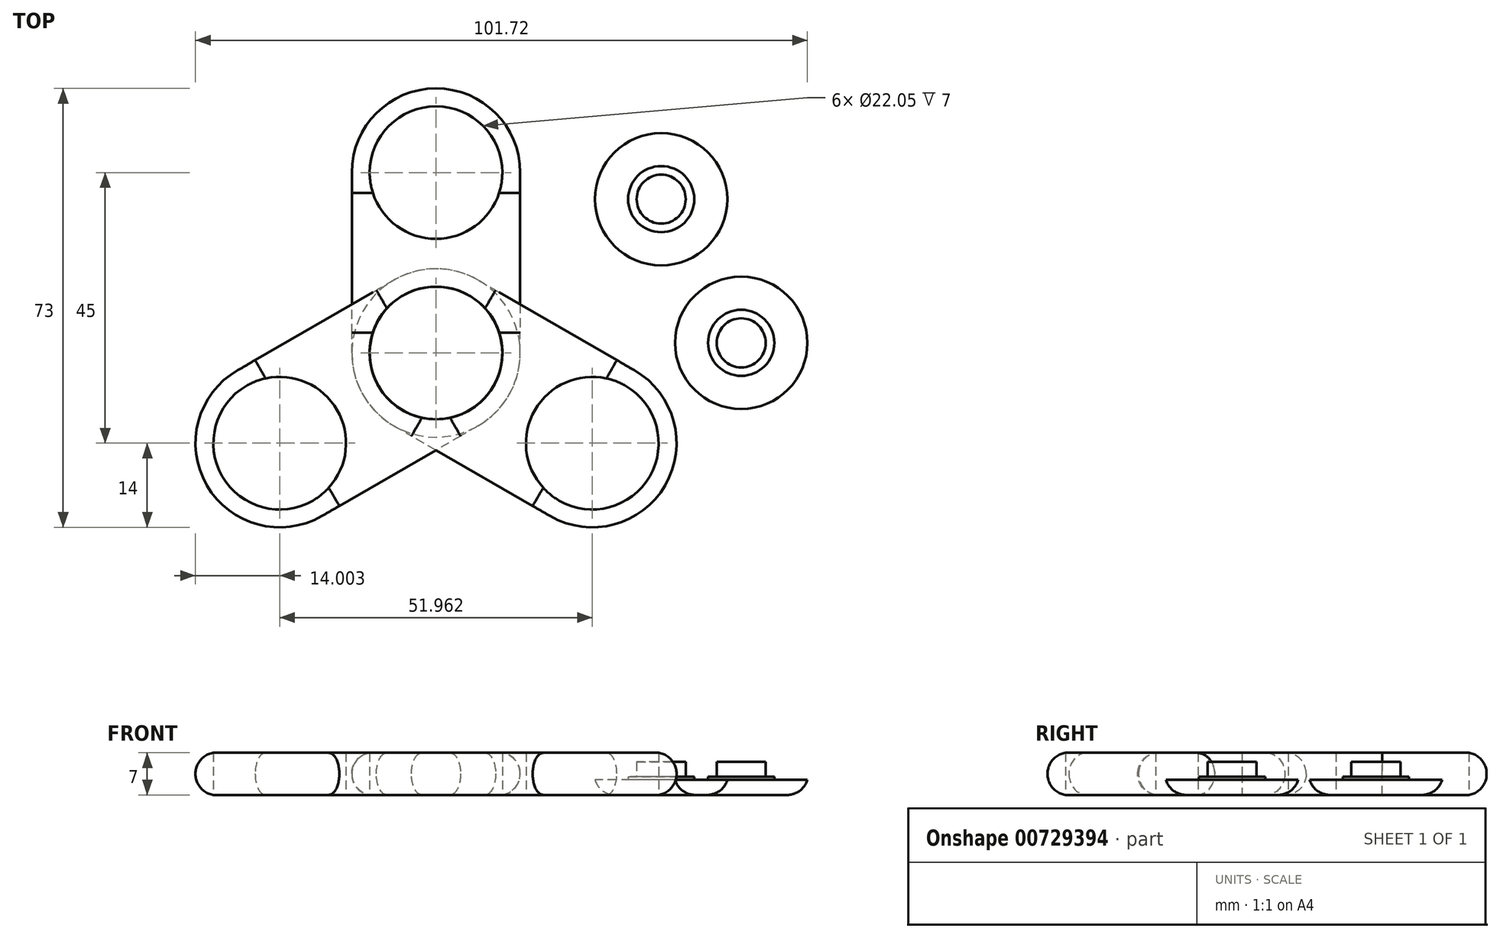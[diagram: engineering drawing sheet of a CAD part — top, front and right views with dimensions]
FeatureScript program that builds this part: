
annotation { "Feature Type Name" : "Feature", "Feature Type Description" : "" }
export const myFeature = defineFeature(function(context is Context, id is Id, definition is map)
    precondition{}
    {
        {
            var Q0;
            Q0=qCreatedBy(makeId("Top.planeOp"),FACE);
            var sketch = newSketch(context, id + "F0", { "sketchPlane" : qUnion([Q0])});
            skLineSegment(sketch, "E0.bottom", {"start": v(-13.49, 0) * mm, "end": v(14.51, 0) * mm});
            skLineSegment(sketch, "E0.top", {"start": v(-13.49, 30) * mm, "end": v(14.51, 30) * mm});
            skLineSegment(sketch, "E0.left", {"start": v(-13.49, 0) * mm, "end": v(-13.49, 30) * mm});
            skLineSegment(sketch, "E0.right", {"start": v(14.51, 0) * mm, "end": v(14.51, 30) * mm});
            skCircle(sketch, "E1", {"center": v(0.51, 30) * mm, "radius": 14 * mm});
            skCircle(sketch, "E2", {"center": v(0.51, 30) * mm, "radius": 11.03 * mm});
            skCircle(sketch, "E3", {"center": v(0.51, 0) * mm, "radius": 14 * mm});
            skCircle(sketch, "E4", {"center": v(0.51, 0) * mm, "radius": 11.03 * mm});
            skSolve(sketch);
        }
        {
            var Q0;
            {var subQ1=sQuery(id+"F0.wireOp",EDGE,"E0.top");var subQ3=sQuery(id+"F0.wireOp",EDGE,"E2");var subQ4=makeQuery(id+"F0.imprint","INTERSECT",VERTEX,{"disambiguationData":[OD(0.0)],"derivedFrom":[subQ1,subQ3]});Q0=makeQuery(id+"F0.imprint","IMPRINT",FACE,{"disambiguationData":[TD([[makeQuery(id+"F0.imprint","IMPRINT",EDGE,{"disambiguationData":[TD([[subQ4,-1.0]])],"derivedFrom":subQ3}),-1.0]])]});}
            var Q1;
            {var subQ1=sQuery(id+"F0.wireOp",EDGE,"E0.top");var subQ3=sQuery(id+"F0.wireOp",EDGE,"E2");var subQ4=makeQuery(id+"F0.imprint","INTERSECT",VERTEX,{"disambiguationData":[OD(0.0)],"derivedFrom":[subQ1,subQ3]});Q1=makeQuery(id+"F0.imprint","IMPRINT",FACE,{"disambiguationData":[TD([[makeQuery(id+"F0.imprint","IMPRINT",EDGE,{"disambiguationData":[TD([[subQ4,1.0]])],"derivedFrom":subQ3}),-1.0]])]});}
            var Q2;
            {var subQ0=sQuery(id+"F0.wireOp",EDGE,"E0.left");Q2=makeQuery(id+"F0.imprint","IMPRINT",FACE,{"disambiguationData":[TD([[makeQuery(id+"F0.imprint","IMPRINT",EDGE,{"derivedFrom":subQ0}),-1.0]])]});}
            var Q3;
            {var subQ1=sQuery(id+"F0.wireOp",EDGE,"E0.bottom");var subQ3=sQuery(id+"F0.wireOp",EDGE,"E4");var subQ4=makeQuery(id+"F0.imprint","INTERSECT",VERTEX,{"disambiguationData":[OD(0.0)],"derivedFrom":[subQ1,subQ3]});Q3=makeQuery(id+"F0.imprint","IMPRINT",FACE,{"disambiguationData":[TD([[makeQuery(id+"F0.imprint","IMPRINT",EDGE,{"disambiguationData":[TD([[subQ4,1.0]])],"derivedFrom":subQ3}),-1.0]])]});}
            var Q4;
            {var subQ1=sQuery(id+"F0.wireOp",EDGE,"E0.bottom");var subQ3=sQuery(id+"F0.wireOp",EDGE,"E4");var subQ4=makeQuery(id+"F0.imprint","INTERSECT",VERTEX,{"disambiguationData":[OD(0.0)],"derivedFrom":[subQ1,subQ3]});Q4=makeQuery(id+"F0.imprint","IMPRINT",FACE,{"disambiguationData":[TD([[makeQuery(id+"F0.imprint","IMPRINT",EDGE,{"disambiguationData":[TD([[subQ4,-1.0]])],"derivedFrom":subQ3}),-1.0]])]});}
            extrude(context, id + "F1", {"entities" : qUnion([Q0, Q1, Q2, Q3, Q4]), "depth" : 7 * mm, "offsetDistance" : 25 * mm});
        }
        {
            var Q0;
            Q0=makeQuery(id+"F1.opExtrude","SWEPT_BODY",BODY,{"disambiguationData":[OSD([sQuery(id+"F0.wireOp",EDGE,"E0.left"),sQuery(id+"F0.wireOp",EDGE,"E0.right"),sQuery(id+"F0.wireOp",EDGE,"E1"),sQuery(id+"F0.wireOp",EDGE,"E2"),sQuery(id+"F0.wireOp",EDGE,"E3"),sQuery(id+"F0.wireOp",EDGE,"E4")])]});
            var Q1;
            Q1=makeQuery(id+"F1.opExtrude","CAP_EDGE",EDGE,{"disambiguationData":[OSD([sQuery(id+"F0.wireOp",EDGE,"E4")])],"isStart":false});
            circularPattern(context, id + "F2", {"entities" : qUnion([Q0]), "axis" : qUnion([Q1]), "angle" : 360 * degree, "instanceCount" : 3, "equalSpace" : true});
        }
        {
            var Q0;
            Q0=qCreatedBy(makeId("Top.planeOp"),FACE);
            var sketch = newSketch(context, id + "F3", { "sketchPlane" : qUnion([Q0])});
            skCircle(sketch, "E5", {"center": v(37.95, 25.58) * mm, "radius": 11 * mm});
            skCircle(sketch, "E6", {"center": v(37.95, 25.58) * mm, "radius": 4.08 * mm});
            skCircle(sketch, "E7", {"center": v(37.95, 25.58) * mm, "radius": 5.5 * mm});
            skSolve(sketch);
        }
        {
            var Q0;
            Q0=makeQuery(id+"F3.imprint","IMPRINT",FACE,{"disambiguationData":[TD([[makeQuery(id+"F3.imprint","IMPRINT",EDGE,{"derivedFrom":sQuery(id+"F3.wireOp",EDGE,"E5")}),1.0]])]});
            extrude(context, id + "F4", {"entities" : qUnion([Q0]), "depth" : 2.5 * mm, "offsetDistance" : 25 * mm});
        }
        {
            var Q0;
            Q0=makeQuery(id+"F3.imprint","IMPRINT",FACE,{"disambiguationData":[TD([[makeQuery(id+"F3.imprint","IMPRINT",EDGE,{"derivedFrom":sQuery(id+"F3.wireOp",EDGE,"E6")}),-1.0]])]});
            extrude(context, id + "F5", {"entities" : qUnion([Q0]), "operationType" : NewBodyOperationType.ADD, "depth" : 3 * mm, "offsetDistance" : 25 * mm});
        }
        {
            var Q0;
            Q0=makeQuery(id+"F3.imprint","IMPRINT",FACE,{"disambiguationData":[TD([[makeQuery(id+"F3.imprint","IMPRINT",EDGE,{"derivedFrom":sQuery(id+"F3.wireOp",EDGE,"E6")}),1.0]])]});
            extrude(context, id + "F6", {"entities" : qUnion([Q0]), "operationType" : NewBodyOperationType.ADD, "depth" : 5.5 * mm, "offsetDistance" : 25 * mm});
        }
        {
            var Q0;
            Q0=makeQuery(id+"F2.opPattern","COPY",EDGE,{"derivedFrom":makeQuery(id+"F1.opExtrude","CAP_EDGE",EDGE,{"disambiguationData":[OSD([sQuery(id+"F0.wireOp",EDGE,"E1")])],"isStart":false}),"instanceName":"1"});
            var Q1;
            Q1=makeQuery(id+"F2.opPattern","COPY",EDGE,{"derivedFrom":makeQuery(id+"F1.opExtrude","CAP_EDGE",EDGE,{"disambiguationData":[OSD([sQuery(id+"F0.wireOp",EDGE,"E1")])],"isStart":true}),"instanceName":"1"});
            var Q2;
            Q2=makeQuery(id+"F2.opPattern","COPY",EDGE,{"derivedFrom":makeQuery(id+"F1.opExtrude","CAP_EDGE",EDGE,{"disambiguationData":[OSD([sQuery(id+"F0.wireOp",EDGE,"E0.right")])],"isStart":false}),"instanceName":"2"});
            var Q3;
            Q3=makeQuery(id+"F2.opPattern","COPY",EDGE,{"derivedFrom":makeQuery(id+"F1.opExtrude","CAP_EDGE",EDGE,{"disambiguationData":[OSD([sQuery(id+"F0.wireOp",EDGE,"E0.left")])],"isStart":false}),"instanceName":"1"});
            var Q4;
            Q4=makeQuery(id+"F2.opPattern","COPY",EDGE,{"derivedFrom":makeQuery(id+"F1.opExtrude","CAP_EDGE",EDGE,{"disambiguationData":[OSD([sQuery(id+"F0.wireOp",EDGE,"E0.left")])],"isStart":true}),"instanceName":"1"});
            var Q5;
            Q5=makeQuery(id+"F2.opPattern","COPY",EDGE,{"derivedFrom":makeQuery(id+"F1.opExtrude","CAP_EDGE",EDGE,{"disambiguationData":[OSD([sQuery(id+"F0.wireOp",EDGE,"E0.right")])],"isStart":true}),"instanceName":"2"});
            var Q6;
            Q6=makeQuery(id+"F2.opPattern","COPY",EDGE,{"derivedFrom":makeQuery(id+"F1.opExtrude","CAP_EDGE",EDGE,{"disambiguationData":[OSD([sQuery(id+"F0.wireOp",EDGE,"E1")])],"isStart":false}),"instanceName":"2"});
            var Q7;
            Q7=makeQuery(id+"F2.opPattern","COPY",EDGE,{"derivedFrom":makeQuery(id+"F1.opExtrude","CAP_EDGE",EDGE,{"disambiguationData":[OSD([sQuery(id+"F0.wireOp",EDGE,"E1")])],"isStart":true}),"instanceName":"2"});
            var Q8;
            Q8=makeQuery(id+"F1.opExtrude","CAP_EDGE",EDGE,{"disambiguationData":[OSD([sQuery(id+"F0.wireOp",EDGE,"E0.left")])],"isStart":false});
            var Q9;
            Q9=makeQuery(id+"F1.opExtrude","CAP_EDGE",EDGE,{"disambiguationData":[OSD([sQuery(id+"F0.wireOp",EDGE,"E0.left")])],"isStart":true});
            var Q10;
            Q10=makeQuery(id+"F4.opExtrude","CAP_EDGE",EDGE,{"disambiguationData":[OSD([sQuery(id+"F3.wireOp",EDGE,"E5")])],"isStart":true});
            fillet(context, id + "F7", {"entities" : qUnion([Q0, Q1, Q2, Q3, Q4, Q5, Q6, Q7, Q8, Q9, Q10]), "radius" : 3.5 * mm, "tangentPropagation" : true, "allowEdgeOverflow" : false});
        }
        {
            var Q0;
            Q0=makeQuery(id+"F4.opExtrude","SWEPT_BODY",BODY,{"disambiguationData":[OSD([sQuery(id+"F3.wireOp",EDGE,"E5"),sQuery(id+"F3.wireOp",EDGE,"E7")])]});
            transform(context, id + "F8", {"entities" : qUnion([Q0]), "transformType" : TransformType.TRANSLATION_3D, "dx" : 13.3 * mm, "dy" : -23.9 * mm, "dz" : 0 * mm, "makeCopy" : true});
        }
    });
